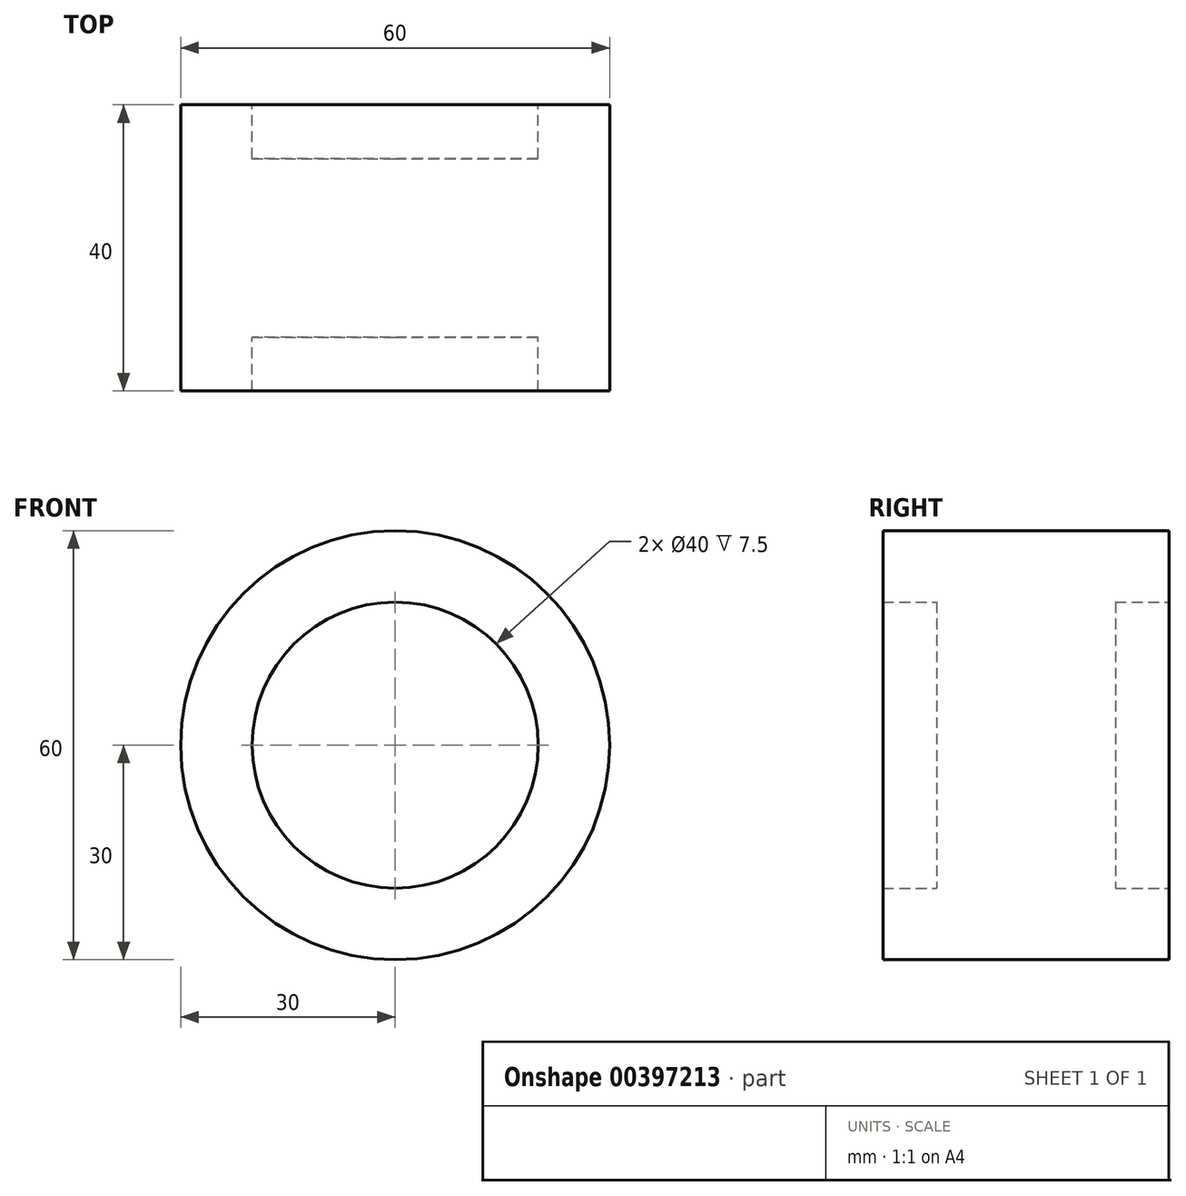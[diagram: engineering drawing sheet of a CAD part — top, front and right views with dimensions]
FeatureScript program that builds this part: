
annotation { "Feature Type Name" : "Feature", "Feature Type Description" : "" }
export const myFeature = defineFeature(function(context is Context, id is Id, definition is map)
    precondition{}
    {
        {
            var Q0;
            Q0=qCreatedBy(makeId("Right.planeOp"),FACE);
            var sketch = newSketch(context, id + "F0", { "sketchPlane" : qUnion([Q0])});
            skLineSegment(sketch, "E0", {"start": v(-12.5, 0) * mm, "end": v(-12.5, 20) * mm});
            skLineSegment(sketch, "E1", {"start": v(-12.5, 20) * mm, "end": v(-20, 20) * mm});
            skLineSegment(sketch, "E2", {"start": v(-20, 20) * mm, "end": v(-20, 30) * mm});
            skLineSegment(sketch, "E3", {"start": v(-20, 30) * mm, "end": v(20, 30) * mm});
            skLineSegment(sketch, "E4", {"start": v(20, 30) * mm, "end": v(20, 20) * mm});
            skLineSegment(sketch, "E5", {"start": v(20, 20) * mm, "end": v(12.5, 20) * mm});
            skLineSegment(sketch, "E6", {"start": v(12.5, 20) * mm, "end": v(12.5, 0) * mm});
            skLineSegment(sketch, "E7", {"start": v(12.5, 0) * mm, "end": v(-12.5, 0) * mm});
            skLineSegment(sketch, "E8", {"start": v(0, 0) * mm, "end": v(0, 30) * mm, "construction": true});
            skSolve(sketch);
        }
        {
            var Q0;
            Q0=makeQuery(id+"F0.imprint","IMPRINT",FACE,{"disambiguationData":[TD([[makeQuery(id+"F0.imprint","IMPRINT",EDGE,{"derivedFrom":sQuery(id+"F0.wireOp",EDGE,"E0")}),-1.0]])]});
            var Q1;
            Q1=sQuery(id+"F0.wireOp",EDGE,"E7");
            revolve(context, id + "F1", {"entities" : qUnion([Q0]), "axis" : qUnion([Q1]), "revolveType" : RevolveType.FULL});
        }
    });
